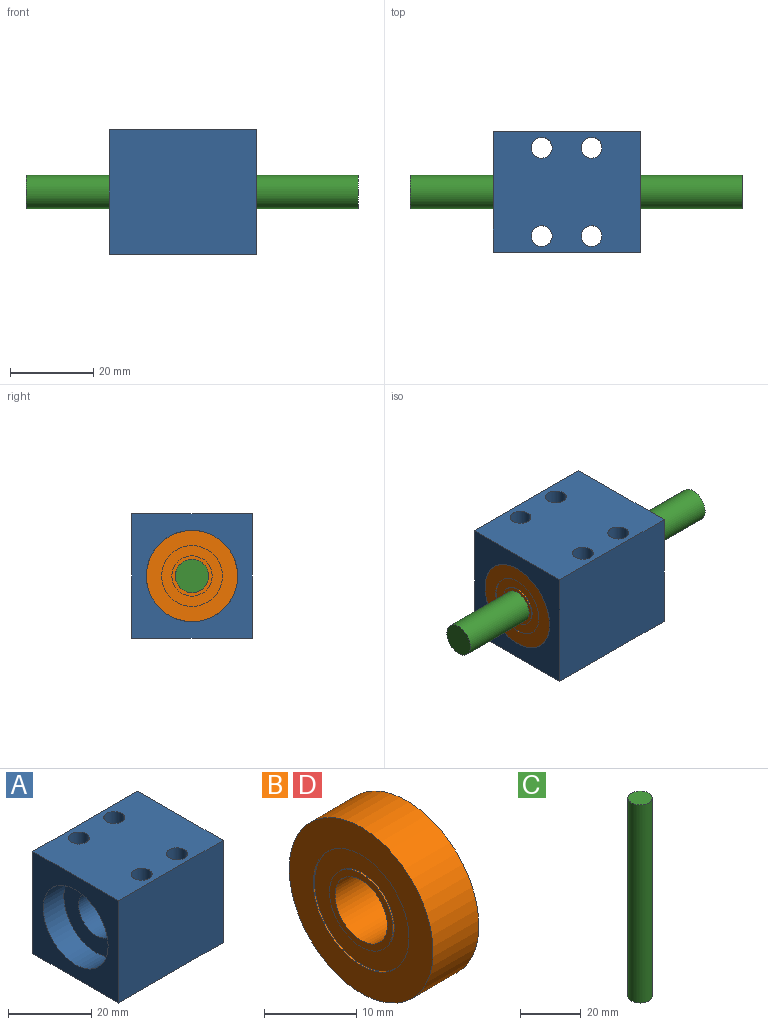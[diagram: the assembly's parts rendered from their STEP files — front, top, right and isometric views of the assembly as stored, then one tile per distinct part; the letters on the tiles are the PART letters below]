
ASSEMBLY  parts=4 mates=3
PART A: 15 faces, bbox 35.5x29x30 mm
  f0: plane 35.5x30mm, normal (0,1,0), area 1065mm2, adj f1,f3,f4,f5
  f1: plane 30x29mm, normal (-1,0,0), area 489.9mm2, adj f0,f2,f4,f5,f6
  f2: plane 35.5x30mm, normal (0,-1,0), area 1065mm2, adj f1,f3,f4,f5
  f3: plane 30x29mm, normal (1,0,0), area 489.9mm2, adj f0,f2,f4,f5,f8
  f4: plane 35.5x29mm, normal (0,0,-1), area 951mm2, adj f0,f1,f2,f3,f11,f12,f13,f14
  f5: plane 35.5x29mm, normal (0,0,1), area 951mm2, adj f0,f1,f2,f3,f11,f12,f13,f14
  f6: cylinder r=11mm len=22mm, axis (-1,0,0), area 483.8mm2, adj f1,f7
  f7: plane 22x22mm, normal (-1,0,0), area 267mm2, adj f6,f10
  f8: cylinder r=11mm len=22mm, axis (1,0,0), area 483.8mm2, adj f3,f9
  f9: plane 22x22mm, normal (1,0,0), area 267mm2, adj f8,f10
  f10: cylinder r=6mm len=21.5mm, axis (1,0,0), area 810.5mm2, adj f7,f9
  f11: cylinder r=2.5mm len=30mm, axis (0,0,1), area 471.2mm2, adj f4,f5
  f12: cylinder r=2.5mm len=30mm, axis (0,0,1), area 471.2mm2, adj f4,f5
  f13: cylinder r=2.5mm len=30mm, axis (0,0,1), area 471.2mm2, adj f4,f5
  f14: cylinder r=2.5mm len=30mm, axis (0,0,1), area 471.2mm2, adj f4,f5
PART B: 12 faces, bbox 7x22x22 mm
  f0: cylinder r=7.33mm len=14.65mm, axis (1,0,0), area 9.2mm2, adj f6,f11
  f1: cylinder r=11mm len=22mm, axis (1,0,0), area 483.8mm2, adj f10,f11
  f2: cylinder r=7.33mm len=14.65mm, axis (1,0,0), area 9.2mm2, adj f9,f10
  f3: cylinder r=4.85mm len=9.7mm, axis (1,0,0), area 6.1mm2, adj f8,f9
  f4: cylinder r=4mm len=8mm, axis (1,0,0), area 175.9mm2, adj f7,f8
  f5: cylinder r=4.85mm len=9.7mm, axis (1,0,0), area 6.1mm2, adj f6,f7
  f6: plane 14.65x14.65mm, normal (-1,0,0), area 94.7mm2, adj f0,f5
  f7: plane 9.7x9.7mm, normal (-1,0,0), area 23.6mm2, adj f4,f5
  f8: plane 9.7x9.7mm, normal (1,0,0), area 23.6mm2, adj f3,f4
  f9: plane 14.65x14.65mm, normal (1,0,0), area 94.7mm2, adj f2,f3
  f10: plane 22x22mm, normal (1,0,0), area 211.6mm2, adj f1,f2
  f11: plane 22x22mm, normal (-1,0,0), area 211.6mm2, adj f0,f1
PART C: 3 faces, bbox 8x8x80 mm
  f0: cylinder r=4mm len=80mm, axis (0,0,1), area 2010.6mm2, adj f1,f2
  f1: plane 8x8mm, normal (0,0,-1), area 50.3mm2, adj f0
  f2: plane 8x8mm, normal (0,0,1), area 50.3mm2, adj f0
PART D: same geometry as B
PLACE A t=(0.34,-17.72,10.78)mm
PLACE B t=(-32.86,-11.45,-4.22)mm
PLACE C rot(axis=(0,1,0),90deg) t=(23.64,-21.04,26.9)mm
PLACE D t=(-4.36,-11.45,-4.22)mm
MATE fastened C.f0 <-> B.f0  axis (1,0,0) through (-56.36,-11.45,-4.22)mm
MATE fastened B.f0 <-> A.f10  axis (-1,0,0) through (-36.36,-11.45,-4.22)mm
MATE fastened D.f0 <-> A.f10  axis (1,0,0) through (-0.86,-11.45,-4.22)mm
